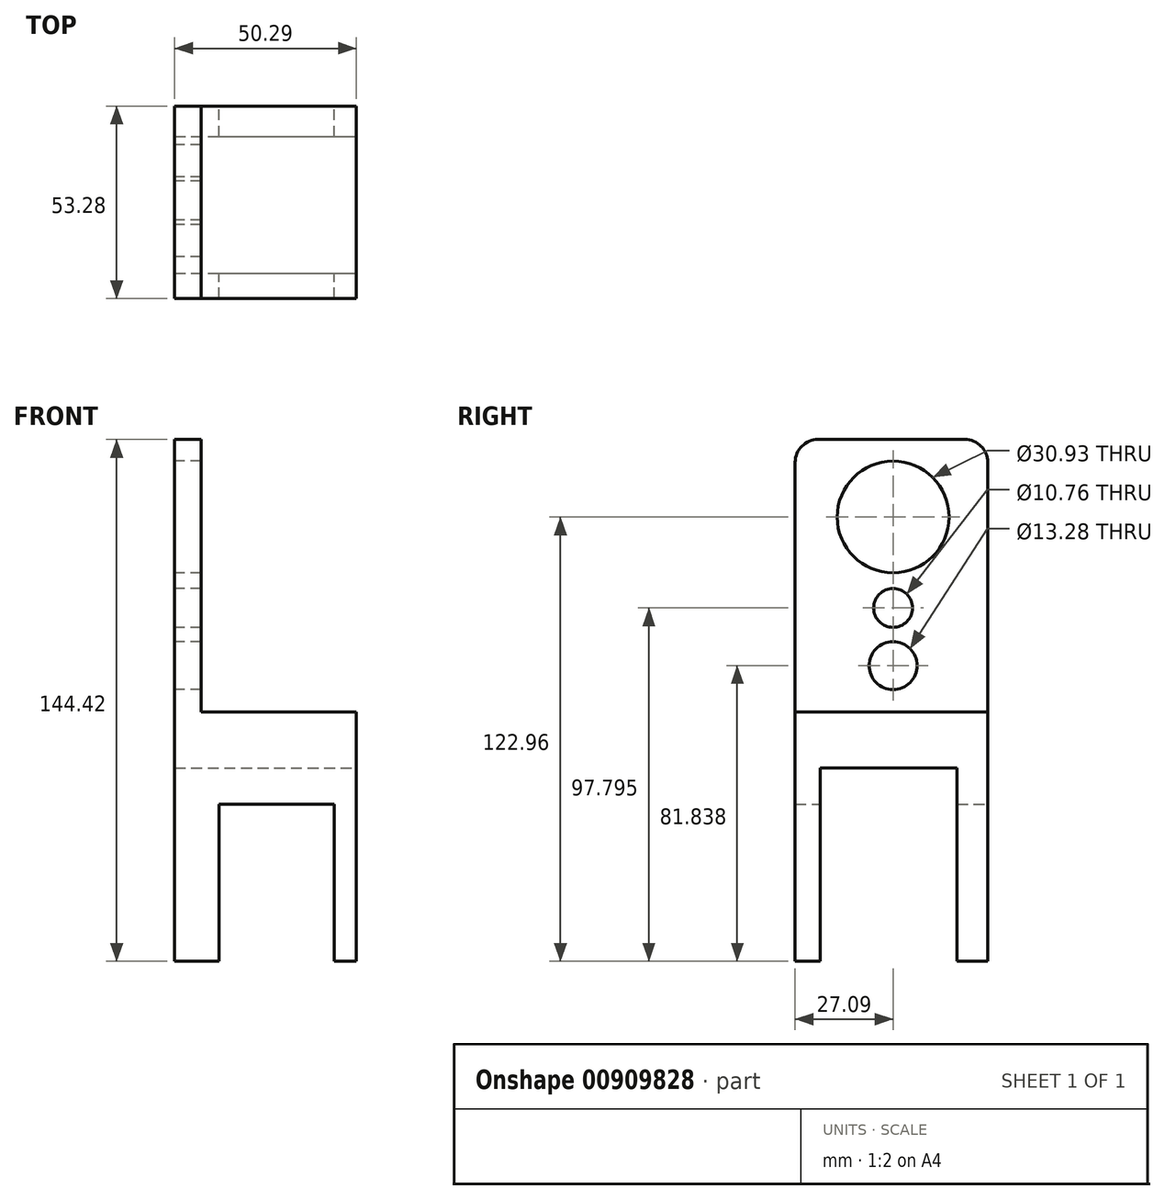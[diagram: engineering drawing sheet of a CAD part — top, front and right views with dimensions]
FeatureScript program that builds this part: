
annotation { "Feature Type Name" : "Feature", "Feature Type Description" : "" }
export const myFeature = defineFeature(function(context is Context, id is Id, definition is map)
    precondition{}
    {
        {
            var Q0;
            Q0=qCreatedBy(makeId("Right.planeOp"),FACE);
            var sketch = newSketch(context, id + "F0", { "sketchPlane" : qUnion([Q0])});
            skLineSegment(sketch, "E0.bottom", {"start": v(-20.74, 85.9) * mm, "end": v(19.84, 85.9) * mm});
            skLineSegment(sketch, "E0.top", {"start": v(-27.09, -58.52) * mm, "end": v(26.2, -58.52) * mm});
            skLineSegment(sketch, "E0.left", {"start": v(-27.09, 79.55) * mm, "end": v(-27.09, -58.52) * mm});
            skLineSegment(sketch, "E0.right", {"start": v(26.2, 79.55) * mm, "end": v(26.2, -58.52) * mm});
            skCircle(sketch, "E1", {"center": v(0, 64.44) * mm, "radius": 15.46 * mm});
            skPoint(sketch, "E2.visualSharp", {"position": v(-27.09, 85.9) * mm});
            skArc(sketch, "E2.filletArc", {"start": v(-20.74, 85.9) * mm, "mid": v(-25.23, 84.04) * mm, "end": v(-27.09, 79.55) * mm});
            skPoint(sketch, "E3.visualSharp", {"position": v(26.2, 85.9) * mm});
            skArc(sketch, "E3.filletArc", {"start": v(26.2, 79.55) * mm, "mid": v(24.33, 84.04) * mm, "end": v(19.84, 85.9) * mm});
            skCircle(sketch, "E4", {"center": v(0, 39.28) * mm, "radius": 5.38 * mm});
            skCircle(sketch, "E5", {"center": v(0, 23.32) * mm, "radius": 6.64 * mm});
            skSolve(sketch);
        }
        {
            var Q0;
            Q0=makeQuery(id+"F0.imprint","IMPRINT",FACE,{"disambiguationData":[TD([[makeQuery(id+"F0.imprint","IMPRINT",EDGE,{"derivedFrom":sQuery(id+"F0.wireOp",EDGE,"E0.bottom")}),-1.0]])]});
            var Q1;
            Q1 = qSketchRegion(id + "F2", true);
            extrude(context, id + "F1", {"entities" : qUnion([Q0, Q1]), "endBound" : BoundingType.SYMMETRIC, "depth" : 7.37 * mm, "offsetDistance" : 25.4 * mm});
        }
        {
            var Q0;
            Q0=makeQuery(id+"F1.opExtrude","CAP_FACE",FACE,{"disambiguationData":[OSD([sQuery(id+"F0.wireOp",EDGE,"E0.bottom"),sQuery(id+"F0.wireOp",EDGE,"E0.top"),sQuery(id+"F0.wireOp",EDGE,"E0.left"),sQuery(id+"F0.wireOp",EDGE,"E0.right"),sQuery(id+"F0.wireOp",EDGE,"E1"),sQuery(id+"F0.wireOp",EDGE,"E2.filletArc"),sQuery(id+"F0.wireOp",EDGE,"E3.filletArc")])],"isStart":false});
            var sketch = newSketch(context, id + "F2", { "sketchPlane" : qUnion([Q0])});
            skLineSegment(sketch, "E6.bottom", {"start": v(-27.09, 10.51) * mm, "end": v(26.2, 10.51) * mm});
            skLineSegment(sketch, "E6.top", {"start": v(-27.09, -58.52) * mm, "end": v(26.2, -58.52) * mm});
            skLineSegment(sketch, "E6.left", {"start": v(-27.09, 10.51) * mm, "end": v(-27.09, -58.52) * mm});
            skLineSegment(sketch, "E6.right", {"start": v(26.2, 10.51) * mm, "end": v(26.2, -58.52) * mm});
            skSolve(sketch);
        }
        {
            var Q0;
            Q0=makeQuery(id+"F2.imprint","IMPRINT",FACE,{"disambiguationData":[TD([[makeQuery(id+"F2.imprint","IMPRINT",EDGE,{"derivedFrom":sQuery(id+"F2.wireOp",EDGE,"E6.bottom")}),-1.0]])]});
            extrude(context, id + "F3", {"entities" : qUnion([Q0]), "operationType" : NewBodyOperationType.ADD, "depth" : 42.93 * mm, "offsetDistance" : 25.4 * mm});
        }
        {
            var Q0;
            Q0=makeQuery(id+"F3.opExtrude","CAP_FACE",FACE,{"disambiguationData":[OSD([sQuery(id+"F2.wireOp",EDGE,"E6.bottom"),sQuery(id+"F2.wireOp",EDGE,"E6.top"),sQuery(id+"F2.wireOp",EDGE,"E6.left"),sQuery(id+"F2.wireOp",EDGE,"E6.right")])],"isStart":false});
            var sketch = newSketch(context, id + "F4", { "sketchPlane" : qUnion([Q0])});
            skLineSegment(sketch, "E7.bottom", {"start": v(-20.14, -5.02) * mm, "end": v(17.7, -5.02) * mm});
            skLineSegment(sketch, "E7.top", {"start": v(-20.14, -58.52) * mm, "end": v(17.7, -58.52) * mm});
            skLineSegment(sketch, "E7.left", {"start": v(-20.14, -5.02) * mm, "end": v(-20.14, -58.52) * mm});
            skLineSegment(sketch, "E7.right", {"start": v(17.7, -5.02) * mm, "end": v(17.7, -58.52) * mm});
            skSolve(sketch);
        }
        {
            var Q0;
            Q0=makeQuery(id+"F4.imprint","IMPRINT",FACE,{"disambiguationData":[TD([[makeQuery(id+"F4.imprint","IMPRINT",EDGE,{"derivedFrom":sQuery(id+"F4.wireOp",EDGE,"E7.bottom")}),-1.0]])]});
            extrude(context, id + "F5", {"entities" : qUnion([Q0]), "operationType" : NewBodyOperationType.REMOVE, "endBound" : BoundingType.THROUGH_ALL, "oppositeDirection" : true, "depth" : 25.4 * mm, "offsetDistance" : 25.4 * mm});
        }
        {
            var Q0;
            Q0=makeQuery(id+"F3.boolean.opBoolean","MERGE",FACE,{"derivedFrom":[makeQuery(id+"F1.opExtrude","SWEPT_FACE",FACE,{"disambiguationData":[OSD([sQuery(id+"F0.wireOp",EDGE,"E0.right")])]}),makeQuery(id+"F3.opExtrude","SWEPT_FACE",FACE,{"disambiguationData":[OSD([sQuery(id+"F2.wireOp",EDGE,"E6.right")])]})]});
            var sketch = newSketch(context, id + "F6", { "sketchPlane" : qUnion([Q0])});
            skLineSegment(sketch, "E8.bottom", {"start": v(-40.47, -15) * mm, "end": v(-8.55, -15) * mm});
            skLineSegment(sketch, "E8.top", {"start": v(-40.47, -58.52) * mm, "end": v(-8.55, -58.52) * mm});
            skLineSegment(sketch, "E8.left", {"start": v(-40.47, -15) * mm, "end": v(-40.47, -58.52) * mm});
            skLineSegment(sketch, "E8.right", {"start": v(-8.55, -15) * mm, "end": v(-8.55, -58.52) * mm});
            skSolve(sketch);
        }
        {
            var Q0;
            Q0=makeQuery(id+"F6.imprint","IMPRINT",FACE,{"disambiguationData":[TD([[makeQuery(id+"F6.imprint","IMPRINT",EDGE,{"derivedFrom":sQuery(id+"F6.wireOp",EDGE,"E8.bottom")}),-1.0]])]});
            extrude(context, id + "F7", {"entities" : qUnion([Q0]), "operationType" : NewBodyOperationType.REMOVE, "endBound" : BoundingType.THROUGH_ALL, "oppositeDirection" : true, "depth" : 25.4 * mm, "offsetDistance" : 25.4 * mm});
        }
    });
